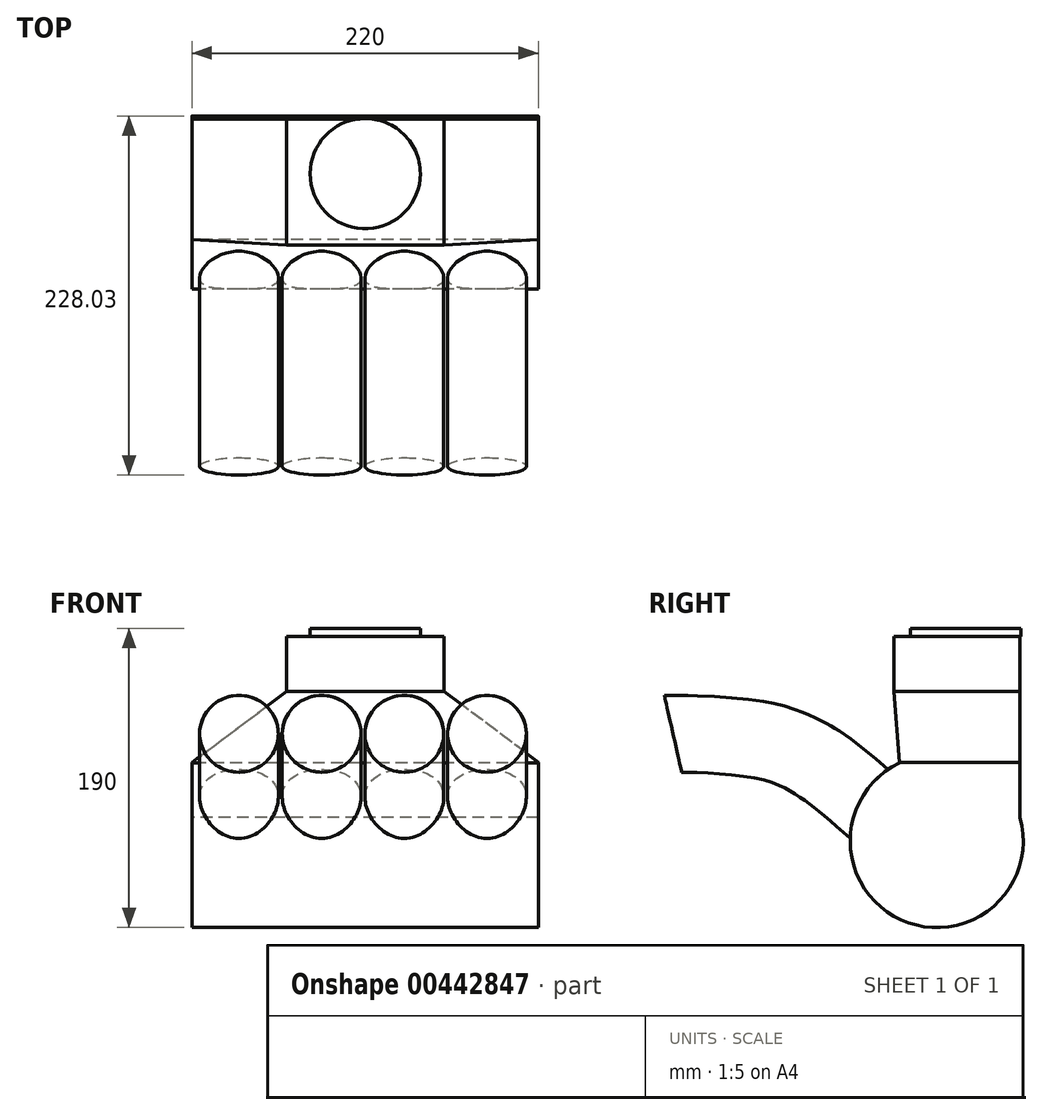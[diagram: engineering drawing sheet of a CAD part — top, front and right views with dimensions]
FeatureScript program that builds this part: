
annotation { "Feature Type Name" : "Feature", "Feature Type Description" : "" }
export const myFeature = defineFeature(function(context is Context, id is Id, definition is map)
    precondition{}
    {
        {
            var Q0;
            Q0=qCreatedBy(makeId("Right.planeOp"),FACE);
            var sketch = newSketch(context, id + "F0", { "sketchPlane" : qUnion([Q0])});
            skArc(sketch, "E0", {"start": v(-5.94, 54.68) * mm, "mid": v(-54.91, -3.07) * mm, "end": v(0.2, -55) * mm});
            skArc(sketch, "E1", {"start": v(-23.6, 49.68) * mm, "mid": v(-34.66, -42.7) * mm, "end": v(53.47, -12.87) * mm});
            skArc(sketch, "E2", {"start": v(50, 22.92) * mm, "mid": v(27.16, 47.83) * mm, "end": v(-5.94, 54.68) * mm});
            skLineSegment(sketch, "E3", {"start": v(-4.37, 54.83) * mm, "end": v(-52.92, 15) * mm, "construction": true});
            skLineSegment(sketch, "E4", {"start": v(-52.92, 15) * mm, "end": v(-52.92, 0) * mm, "construction": true});
            skLineSegment(sketch, "E5", {"start": v(-52.92, 15) * mm, "end": v(52.92, 15) * mm, "construction": true});
            skLineSegment(sketch, "E6", {"start": v(52.92, 15) * mm, "end": v(52.92, 0) * mm, "construction": true});
            skLineSegment(sketch, "E7", {"start": v(50, 22.92) * mm, "end": v(50, 22.92) * mm});
            skPoint(sketch, "E8.startSnap0", {"position": v(5.75, -54.7) * mm});
            skLineSegment(sketch, "E9", {"start": v(52.92, 130) * mm, "end": v(52.92, 15) * mm});
            skLineSegment(sketch, "E10", {"start": v(52.92, 130) * mm, "end": v(-27.08, 130) * mm});
            skLineSegment(sketch, "E11", {"start": v(-27.08, 130) * mm, "end": v(-27.08, 95) * mm});
            skLineSegment(sketch, "E12", {"start": v(-27.08, 95) * mm, "end": v(52.92, 95) * mm, "construction": true});
            skPoint(sketch, "E13.visualSharp", {"position": v(-4.37, 54.83) * mm});
            skArc(sketch, "E14", {"start": v(0.2, -55) * mm, "mid": v(54.95, 2.28) * mm, "end": v(-4.37, 54.83) * mm});
            skLineSegment(sketch, "E15", {"start": v(-27.08, 95) * mm, "end": v(-23.6, 49.68) * mm});
            skSolve(sketch);
        }
        {
            var Q0;
            Q0=qSketchRegion(id+"F0",true);
            extrude(context, id + "F1", {"entities" : qUnion([Q0]), "depth" : 220 * mm, "offsetDistance" : 25 * mm, "symmetric" : true});
        }
        {
            var Q0;
            Q0=makeQuery(id+"F1.opExtrude","SWEPT_FACE",FACE,{"disambiguationData":[OSD([sQuery(id+"F0.wireOp",EDGE,"E11")])]});
            cPlane(context, id + "F2", {"entities" : qUnion([Q0]), "cplaneType" : CPlaneType.OFFSET, "offset" : 0 * mm, "width" : 150 * mm, "height" : 150 * mm});
        }
        {
            var Q0;
            Q0=qCreatedBy(id+"F2.planeOp",FACE);
            var sketch = newSketch(context, id + "F3", { "sketchPlane" : qUnion([Q0])});
            skLineSegment(sketch, "E16", {"start": v(0, 0) * mm, "end": v(0, 95) * mm, "construction": true});
            skLineSegment(sketch, "E17", {"start": v(0, 0) * mm, "end": v(110, 0) * mm, "construction": true});
            skLineSegment(sketch, "E18", {"start": v(110, 0) * mm, "end": v(110, 95) * mm, "construction": true});
            skLineSegment(sketch, "E19", {"start": v(110, 95) * mm, "end": v(50, 95) * mm});
            skLineSegment(sketch, "E20", {"start": v(50, 95) * mm, "end": v(50, 130) * mm});
            skLineSegment(sketch, "E21", {"start": v(50, 130) * mm, "end": v(110, 130) * mm});
            skLineSegment(sketch, "E22", {"start": v(110, 130) * mm, "end": v(110, 95) * mm});
            skLineSegment(sketch, "E23", {"start": v(0, 0) * mm, "end": v(-110, 0) * mm, "construction": true});
            skLineSegment(sketch, "E24", {"start": v(-110, 0) * mm, "end": v(-110, 95) * mm, "construction": true});
            skLineSegment(sketch, "E25", {"start": v(-110, 95) * mm, "end": v(-50, 95) * mm});
            skLineSegment(sketch, "E26", {"start": v(-110, 95) * mm, "end": v(-110, 130) * mm});
            skLineSegment(sketch, "E27", {"start": v(-110, 130) * mm, "end": v(-50, 130) * mm});
            skLineSegment(sketch, "E28", {"start": v(-50, 130) * mm, "end": v(-50, 95) * mm});
            skLineSegment(sketch, "E29", {"start": v(-50, 95) * mm, "end": v(-110, 50) * mm});
            skLineSegment(sketch, "E30", {"start": v(-110, 95) * mm, "end": v(-110, 50) * mm});
            skLineSegment(sketch, "E31", {"start": v(50, 95) * mm, "end": v(110, 50) * mm});
            skLineSegment(sketch, "E32", {"start": v(110, 50) * mm, "end": v(110, 95) * mm});
            skSolve(sketch);
        }
        {
            var Q0;
            Q0=qSketchRegion(id+"F3",true);
            extrude(context, id + "F4", {"entities" : qUnion([Q0]), "operationType" : NewBodyOperationType.REMOVE, "oppositeDirection" : true, "depth" : 97.2 * mm, "offsetDistance" : 25 * mm});
        }
        {
            var Q0;
            Q0=makeQuery(id+"F1.opExtrude","SWEPT_FACE",FACE,{"disambiguationData":[OSD([sQuery(id+"F0.wireOp",EDGE,"E0"),sQuery(id+"F0.wireOp",EDGE,"E1")])]});
            cPlane(context, id + "F5", {"entities" : qUnion([Q0]), "cplaneType" : CPlaneType.LINE_ANGLE, "offset" : 25 * mm, "angle" : 40 * degree, "width" : 150 * mm, "height" : 150 * mm});
        }
        {
            var Q0;
            Q0=qCreatedBy(makeId("Right.planeOp"),FACE);
            var sketch = newSketch(context, id + "F6", { "sketchPlane" : qUnion([Q0])});
            skFitSpline(sketch, "E33", {"points": [v(0, -25.86) * mm, v(-32.02, 13.34) * mm, v(-61.57, 39.2) * mm, v(-79.86, 51.87) * mm, v(-112.3, 63.92) * mm, v(-167.53, 67.96) * mm], "startDerivative": vector(-88.77, 196.26) * mm, "endDerivative": vector(-121.68, 0.23) * mm});
            skSolve(sketch);
        }
        {
            var Q0;
            Q0=qCreatedBy(id+"F5.planeOp",FACE);
            var sketch = newSketch(context, id + "F7", { "sketchPlane" : qUnion([Q0])});
            skCircle(sketch, "E34", {"center": v(-80.18, -14.09) * mm, "radius": 25 * mm});
            skCircle(sketch, "E35.1.0.0", {"center": v(-27.68, -14.09) * mm, "radius": 25 * mm});
            skCircle(sketch, "E35.2.0.0", {"center": v(24.82, -14.09) * mm, "radius": 25 * mm});
            skCircle(sketch, "E35.3.0.0", {"center": v(77.32, -14.09) * mm, "radius": 25 * mm});
            skLineSegment(sketch, "E35.direction1", {"start": v(-80.18, -14.09) * mm, "end": v(-27.68, -14.09) * mm, "construction": true});
            skSolve(sketch);
        }
        {
            var Q0;
            Q0 = qSketchRegion(id + "F7", true);
            var Q1;
            Q1 = qConstructionFilter(qBodyType(qCreatedBy(id + "F6" ,EDGE), BodyType.WIRE), ConstructionObject.NO);
            sweep(context, id + "F8", {"operationType" : NewBodyOperationType.ADD, "profiles" : qUnion([Q0]), "path" : qUnion([Q1])});
        }
        {
            var Q0;
            Q0=makeQuery(id+"F1.opExtrude","SWEPT_FACE",FACE,{"disambiguationData":[OSD([sQuery(id+"F0.wireOp",EDGE,"E10")])]});
            cPlane(context, id + "F9", {"entities" : qUnion([Q0]), "cplaneType" : CPlaneType.OFFSET, "offset" : 0 * mm, "width" : 150 * mm, "height" : 150 * mm});
        }
        {
            var Q0;
            Q0=qCreatedBy(id+"F9.planeOp",FACE);
            var sketch = newSketch(context, id + "F10", { "sketchPlane" : qUnion([Q0])});
            skCircle(sketch, "E36", {"center": v(0, 18.3) * mm, "radius": 35 * mm});
            skSolve(sketch);
        }
        {
            var Q0;
            Q0=qSketchRegion(id+"F10",true);
            extrude(context, id + "F11", {"entities" : qUnion([Q0]), "operationType" : NewBodyOperationType.ADD, "depth" : 5 * mm, "offsetDistance" : 25 * mm});
        }
    });
